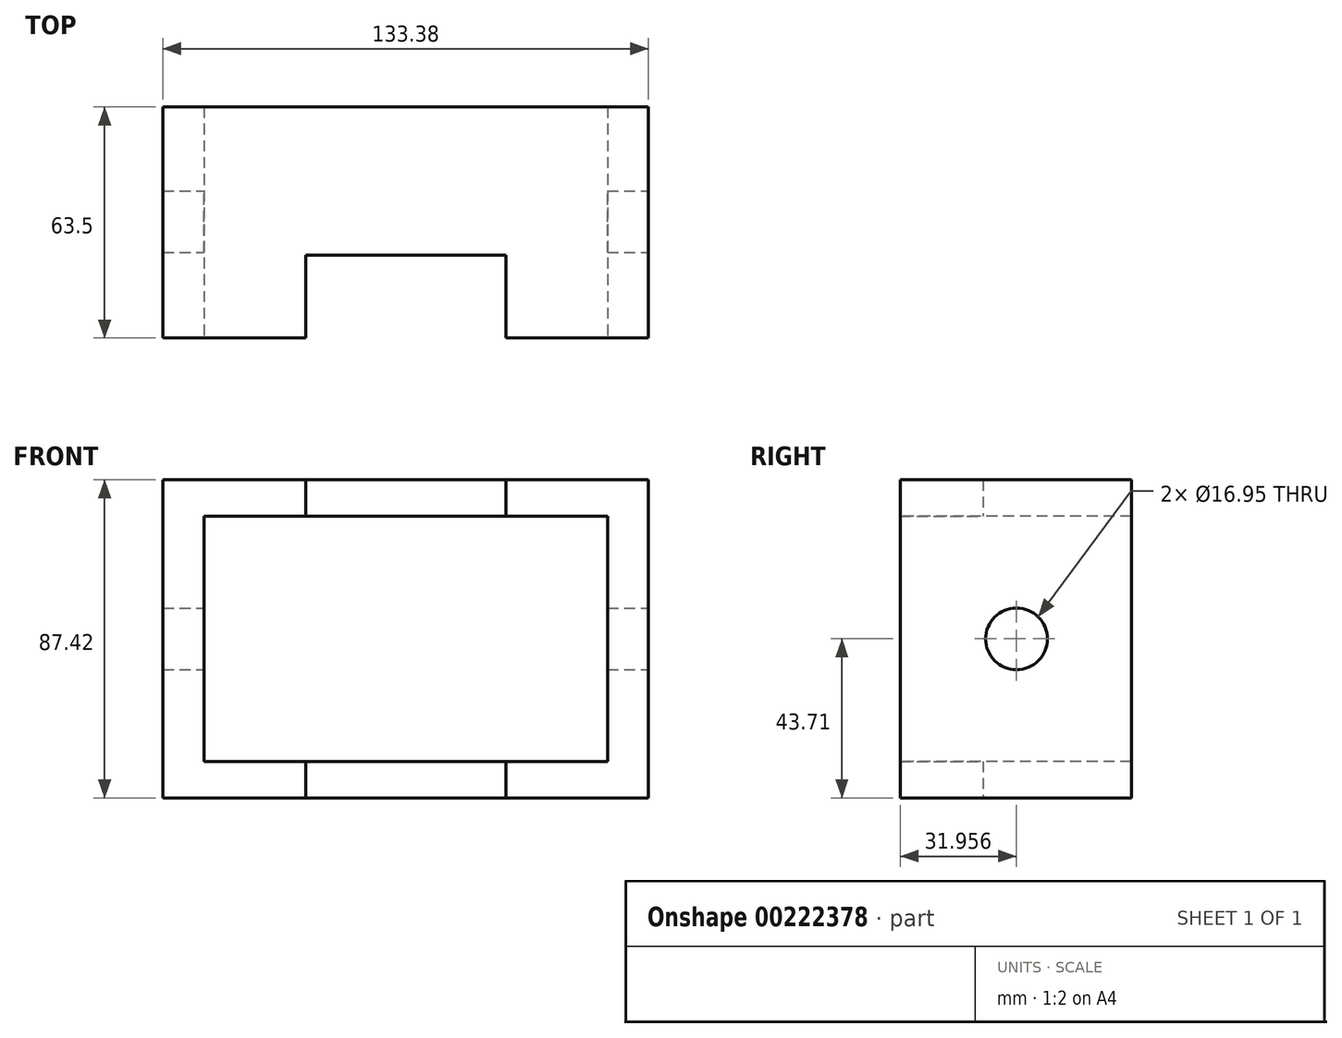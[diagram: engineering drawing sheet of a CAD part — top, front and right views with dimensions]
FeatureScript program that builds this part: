
annotation { "Feature Type Name" : "Feature", "Feature Type Description" : "" }
export const myFeature = defineFeature(function(context is Context, id is Id, definition is map)
    precondition{}
    {
        {
            var Q0;
            Q0=qCreatedBy(makeId("Front.planeOp"),FACE);
            var sketch = newSketch(context, id + "F0", { "sketchPlane" : qUnion([Q0])});
            skLineSegment(sketch, "E0.bottom", {"start": v(66.7, -43.7) * mm, "end": v(-66.7, -43.7) * mm});
            skLineSegment(sketch, "E0.top", {"start": v(66.7, 43.7) * mm, "end": v(-66.7, 43.7) * mm});
            skLineSegment(sketch, "E0.left", {"start": v(66.7, -43.7) * mm, "end": v(66.7, 43.7) * mm});
            skLineSegment(sketch, "E0.right", {"start": v(-66.7, -43.7) * mm, "end": v(-66.7, 43.7) * mm});
            skPoint(sketch, "E0.middle", {"position": v(0, 0) * mm});
            skSolve(sketch);
        }
        {
            var Q0;
            Q0=makeQuery(id+"F0.imprint","IMPRINT",FACE,{"disambiguationData":[TD([[makeQuery(id+"F0.imprint","IMPRINT",EDGE,{"derivedFrom":sQuery(id+"F0.wireOp",EDGE,"E0.bottom")}),-1.0]])]});
            extrude(context, id + "F1", {"entities" : qUnion([Q0]), "depth" : 63.5 * mm});
        }
        {
            var Q0;
            Q0=makeQuery(id+"F1.opExtrude","CAP_FACE",FACE,{"disambiguationData":[OSD([sQuery(id+"F0.wireOp",EDGE,"E0.bottom"),sQuery(id+"F0.wireOp",EDGE,"E0.top"),sQuery(id+"F0.wireOp",EDGE,"E0.left"),sQuery(id+"F0.wireOp",EDGE,"E0.right")])],"isStart":false});
            var sketch = newSketch(context, id + "F4", { "sketchPlane" : qUnion([Q0])});
            skLineSegment(sketch, "E1.bottom", {"start": v(55.41, -33.67) * mm, "end": v(-55.41, -33.67) * mm});
            skLineSegment(sketch, "E1.top", {"start": v(55.41, 33.67) * mm, "end": v(-55.41, 33.67) * mm});
            skLineSegment(sketch, "E1.left", {"start": v(55.41, -33.67) * mm, "end": v(55.41, 33.67) * mm});
            skLineSegment(sketch, "E1.right", {"start": v(-55.41, -33.67) * mm, "end": v(-55.41, 33.67) * mm});
            skPoint(sketch, "E1.middle", {"position": v(0, 0) * mm});
            skSolve(sketch);
        }
        {
            var Q0;
            Q0=makeQuery(id+"F4.imprint","IMPRINT",FACE,{"disambiguationData":[TD([[makeQuery(id+"F4.imprint","IMPRINT",EDGE,{"derivedFrom":sQuery(id+"F4.wireOp",EDGE,"E1.bottom")}),-1.0]])]});
            extrude(context, id + "F5", {"entities" : qUnion([Q0]), "operationType" : NewBodyOperationType.REMOVE, "endBound" : BoundingType.THROUGH_ALL, "oppositeDirection" : true, "depth" : 25.4 * mm});
        }
        {
            var Q0;
            Q0=makeQuery(id+"F1.opExtrude","SWEPT_FACE",FACE,{"disambiguationData":[OSD([sQuery(id+"F0.wireOp",EDGE,"E0.bottom")])]});
            var sketch = newSketch(context, id + "F6", { "sketchPlane" : qUnion([Q0])});
            skLineSegment(sketch, "E2.bottom", {"start": v(27.5, 40.76) * mm, "end": v(-27.5, 40.76) * mm});
            skLineSegment(sketch, "E2.top", {"start": v(27.5, 86.24) * mm, "end": v(-27.5, 86.24) * mm});
            skLineSegment(sketch, "E2.left", {"start": v(27.5, 40.76) * mm, "end": v(27.5, 86.24) * mm});
            skLineSegment(sketch, "E2.right", {"start": v(-27.5, 40.76) * mm, "end": v(-27.5, 86.24) * mm});
            skPoint(sketch, "E2.middle", {"position": v(0, 63.5) * mm});
            skSolve(sketch);
        }
        {
            var Q0;
            {var subQ0=sQuery(id+"F6.wireOp",EDGE,"E2.top");Q0=makeQuery(id+"F6.imprint","IMPRINT",FACE,{"disambiguationData":[TD([[makeQuery(id+"F6.imprint","IMPRINT",EDGE,{"derivedFrom":subQ0}),1.0]])]});}
            var Q1;
            {var subQ0=sQuery(id+"F6.wireOp",EDGE,"E2.bottom");Q1=makeQuery(id+"F6.imprint","IMPRINT",FACE,{"disambiguationData":[TD([[makeQuery(id+"F6.imprint","IMPRINT",EDGE,{"derivedFrom":subQ0}),-1.0]])]});}
            extrude(context, id + "F2", {"entities" : qUnion([Q0, Q1]), "operationType" : NewBodyOperationType.REMOVE, "endBound" : BoundingType.THROUGH_ALL, "oppositeDirection" : true, "depth" : 25.4 * mm});
        }
        {
            var Q0;
            Q0=makeQuery(id+"F1.opExtrude","SWEPT_FACE",FACE,{"disambiguationData":[OSD([sQuery(id+"F0.wireOp",EDGE,"E0.left")])]});
            var sketch = newSketch(context, id + "F3", { "sketchPlane" : qUnion([Q0])});
            skCircle(sketch, "E3", {"center": v(-31.54, 0) * mm, "radius": 8.48 * mm});
            skPoint(sketch, "E3.centerSnap0", {"position": v(-63.5, 0) * mm});
            skSolve(sketch);
        }
        {
            var Q0;
            Q0=makeQuery(id+"F3.imprint","IMPRINT",FACE,{"disambiguationData":[TD([[makeQuery(id+"F3.imprint","IMPRINT",EDGE,{"derivedFrom":sQuery(id+"F3.wireOp",EDGE,"E3")}),1.0]])]});
            extrude(context, id + "F7", {"entities" : qUnion([Q0]), "operationType" : NewBodyOperationType.REMOVE, "endBound" : BoundingType.THROUGH_ALL, "oppositeDirection" : true, "depth" : 25.4 * mm});
        }
    });
